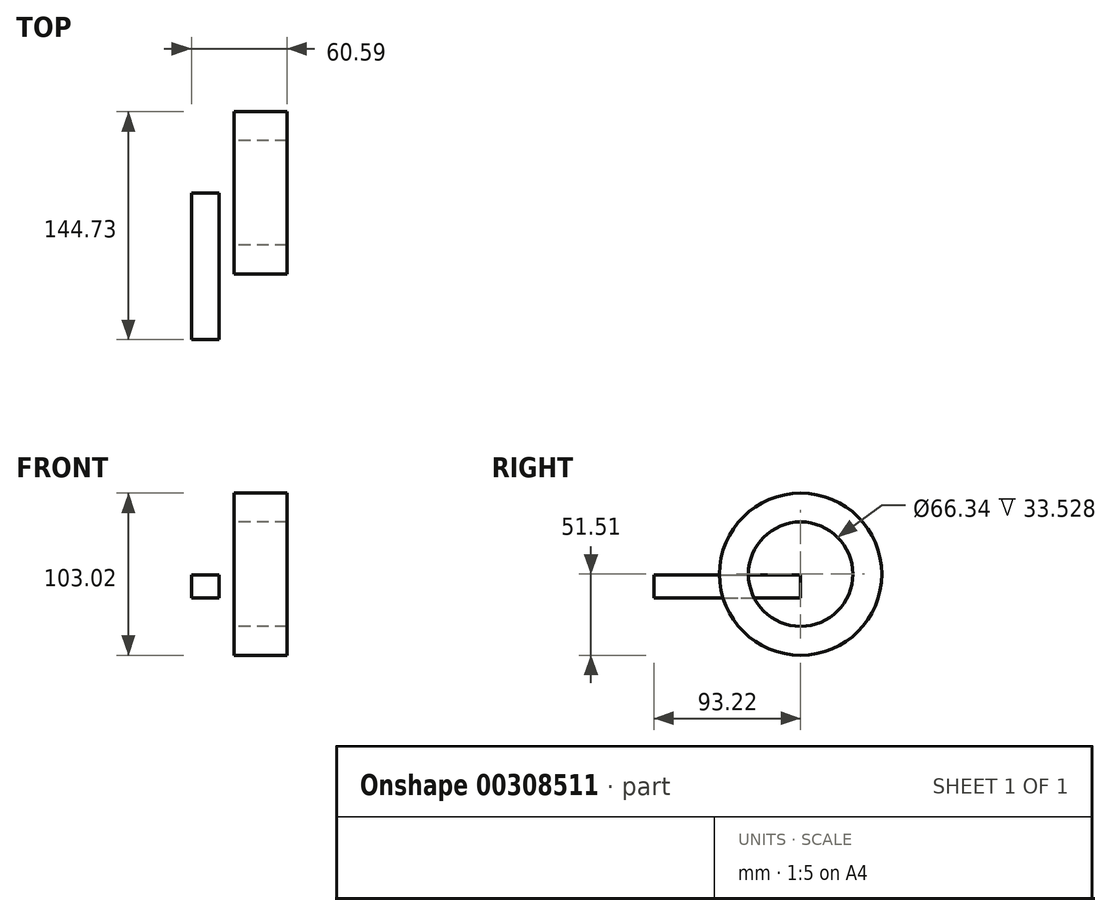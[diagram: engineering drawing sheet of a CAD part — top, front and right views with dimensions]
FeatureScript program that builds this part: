
annotation { "Feature Type Name" : "Feature", "Feature Type Description" : "" }
export const myFeature = defineFeature(function(context is Context, id is Id, definition is map)
    precondition{}
    {
        {
            var Q0;
            Q0=qCreatedBy(makeId("Right.planeOp"),FACE);
            var sketch = newSketch(context, id + "F0", { "sketchPlane" : qUnion([Q0])});
            skCircle(sketch, "E0", {"center": v(0, 0) * mm, "radius": 51.5 * mm});
            skCircle(sketch, "E1", {"center": v(0, 0) * mm, "radius": 33.17 * mm});
            skSolve(sketch);
        }
        {
            var Q0;
            Q0 = qSketchRegion(id + "F0", true);
            extrude(context, id + "F1", {"entities" : qUnion([Q0]), "depth" : 25.4 * mm});
        }
        {
            var Q0;
            Q0=makeQuery(id+"F1.opExtrude","CAP_FACE",FACE,{"disambiguationData":[OSD([sQuery(id+"F0.wireOp",EDGE,"E0"),sQuery(id+"F0.wireOp",EDGE,"E1")])],"isStart":true});
            extrude(context, id + "F2", {"entities" : qUnion([Q0]), "operationType" : NewBodyOperationType.ADD, "depth" : 8.13 * mm});
        }
        {
            var Q0;
            Q0=qCreatedBy(makeId("Front.planeOp"),FACE);
            var sketch = newSketch(context, id + "F3", { "sketchPlane" : qUnion([Q0])});
            skLineSegment(sketch, "E2.bottom", {"start": v(-17.72, -15.02) * mm, "end": v(-35.19, -15.02) * mm});
            skLineSegment(sketch, "E2.top", {"start": v(-17.72, -0.4) * mm, "end": v(-35.19, -0.4) * mm});
            skLineSegment(sketch, "E2.left", {"start": v(-17.72, -15.02) * mm, "end": v(-17.72, -0.4) * mm});
            skLineSegment(sketch, "E2.right", {"start": v(-35.19, -15.02) * mm, "end": v(-35.19, -0.4) * mm});
            skPoint(sketch, "E2.middle", {"position": v(-26.45, -7.71) * mm});
            skSolve(sketch);
        }
        {
            var Q0;
            Q0 = qSketchRegion(id + "F3", true);
            extrude(context, id + "F4", {"entities" : qUnion([Q0]), "depth" : 93.22 * mm});
        }
    });
